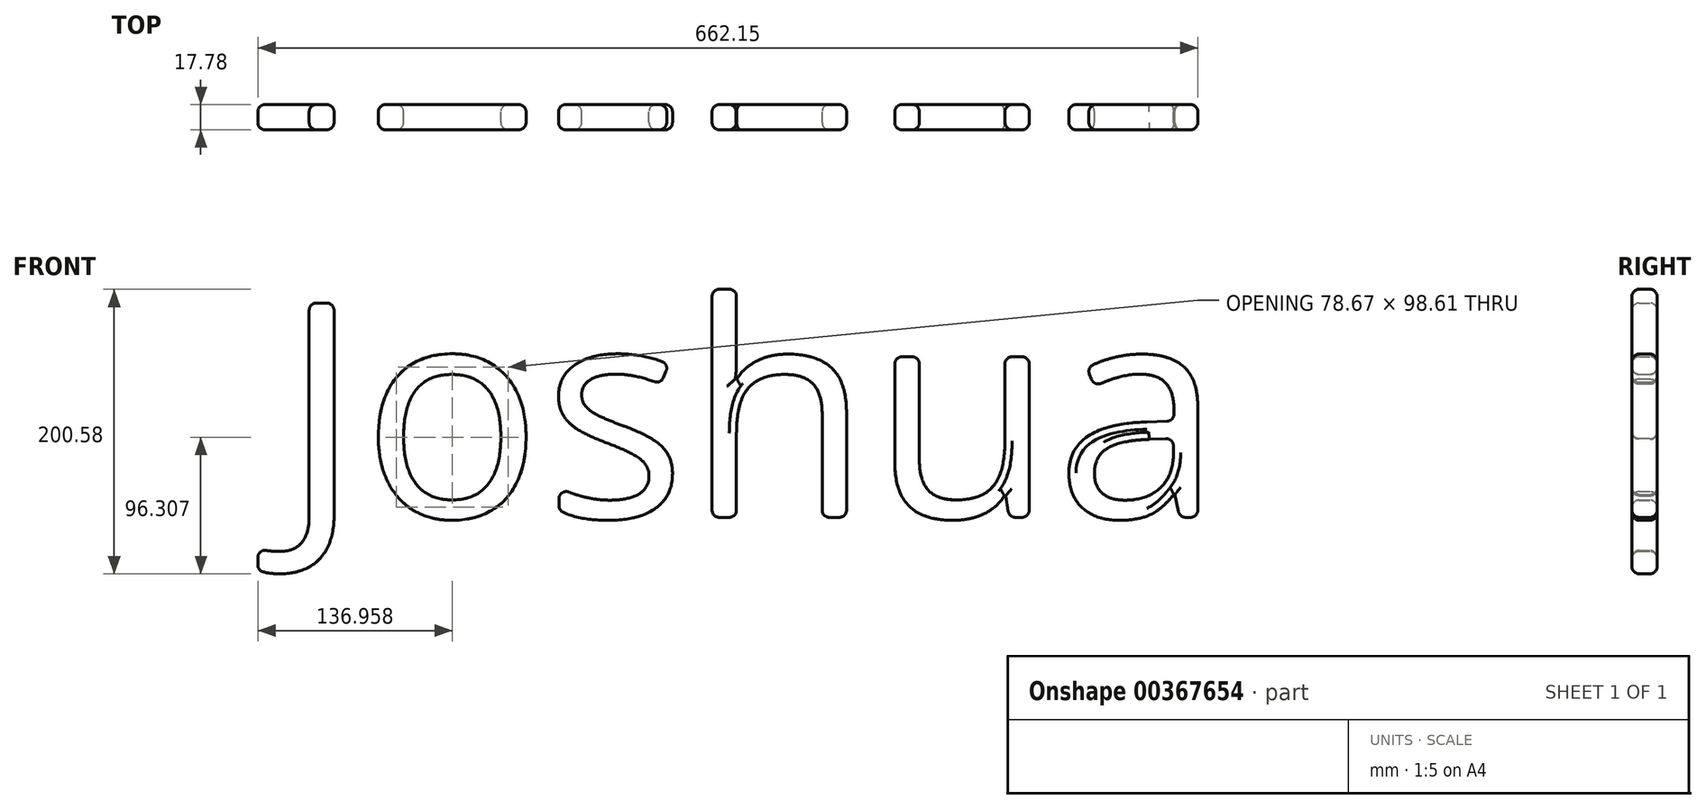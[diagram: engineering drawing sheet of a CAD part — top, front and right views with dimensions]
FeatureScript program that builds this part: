
annotation { "Feature Type Name" : "Feature", "Feature Type Description" : "" }
export const myFeature = defineFeature(function(context is Context, id is Id, definition is map)
    precondition{}
    {
        {
            var Q0;
            Q0=qCreatedBy(makeId("Front.planeOp"),FACE);
            var sketch = newSketch(context, id + "F0", { "sketchPlane" : qUnion([Q0])});
            skText(sketch, "E0", { "text": "Joshua", "fontName": "OpenSans-Regular.ttf"});
            const initialGuessF0  = {"E0": [-0.30372, -0.07697, 1, 0, 0.15237]};
            skSetInitialGuess(sketch, initialGuessF0);
            skSolve(sketch);
        }
        {
            var Q0;
            Q0=makeQuery(id+"F0.imprint","IMPRINT",FACE,{"disambiguationData":[TD([[makeQuery(id+"F0.imprint","IMPRINT",EDGE,{"derivedFrom":sQuery(id+"F0.wireOp",EDGE,"E0.sketch_text.stroke-0")}),-1.0]])]});
            var Q1;
            Q1=makeQuery(id+"F0.imprint","IMPRINT",FACE,{"disambiguationData":[TD([[makeQuery(id+"F0.imprint","IMPRINT",EDGE,{"derivedFrom":sQuery(id+"F0.wireOp",EDGE,"E0.sketch_text.stroke-10")}),-1.0]])]});
            var Q2;
            Q2=makeQuery(id+"F0.imprint","IMPRINT",FACE,{"disambiguationData":[TD([[makeQuery(id+"F0.imprint","IMPRINT",EDGE,{"derivedFrom":sQuery(id+"F0.wireOp",EDGE,"E0.sketch_text.stroke-27")}),-1.0]])]});
            var Q3;
            Q3=makeQuery(id+"F0.imprint","IMPRINT",FACE,{"disambiguationData":[TD([[makeQuery(id+"F0.imprint","IMPRINT",EDGE,{"derivedFrom":sQuery(id+"F0.wireOp",EDGE,"E0.sketch_text.stroke-52")}),-1.0]])]});
            var Q4;
            Q4=makeQuery(id+"F0.imprint","IMPRINT",FACE,{"disambiguationData":[TD([[makeQuery(id+"F0.imprint","IMPRINT",EDGE,{"derivedFrom":sQuery(id+"F0.wireOp",EDGE,"E0.sketch_text.stroke-70")}),-1.0]])]});
            var Q5;
            Q5=makeQuery(id+"F0.imprint","IMPRINT",FACE,{"disambiguationData":[TD([[makeQuery(id+"F0.imprint","IMPRINT",EDGE,{"derivedFrom":sQuery(id+"F0.wireOp",EDGE,"E0.sketch_text.stroke-87")}),-1.0]])]});
            extrude(context, id + "F1", {"entities" : qUnion([Q0, Q1, Q2, Q3, Q4, Q5]), "depth" : 17.78 * mm});
        }
        {
            var Q0;
            Q0=makeQuery(id+"F1.opExtrude","SWEPT_EDGE",EDGE,{"disambiguationData":[OSD([sQuery(id+"F0.wireOp",EDGE,"E0.sketch_text.stroke-5"),sQuery(id+"F0.wireOp",EDGE,"E0.sketch_text.stroke-6")])]});
            var Q1;
            Q1=makeQuery(id+"F1.opExtrude","SWEPT_EDGE",EDGE,{"disambiguationData":[OSD([sQuery(id+"F0.wireOp",EDGE,"E0.sketch_text.stroke-6"),sQuery(id+"F0.wireOp",EDGE,"E0.sketch_text.stroke-7")])]});
            var Q2;
            Q2=makeQuery(id+"F1.opExtrude","CAP_EDGE",EDGE,{"disambiguationData":[OSD([sQuery(id+"F0.wireOp",EDGE,"E0.sketch_text.stroke-0")])],"isStart":false});
            var Q3;
            Q3=makeQuery(id+"F1.opExtrude","CAP_EDGE",EDGE,{"disambiguationData":[OSD([sQuery(id+"F0.wireOp",EDGE,"E0.sketch_text.stroke-2")])],"isStart":true});
            var Q4;
            Q4=makeQuery(id+"F1.opExtrude","CAP_EDGE",EDGE,{"disambiguationData":[OSD([sQuery(id+"F0.wireOp",EDGE,"E0.sketch_text.stroke-2")])],"isStart":false});
            var Q5;
            Q5=makeQuery(id+"F1.opExtrude","SWEPT_EDGE",EDGE,{"disambiguationData":[OSD([sQuery(id+"F0.wireOp",EDGE,"E0.sketch_text.stroke-0"),sQuery(id+"F0.wireOp",EDGE,"E0.sketch_text.stroke-9")])]});
            var Q6;
            Q6=makeQuery(id+"F1.opExtrude","SWEPT_EDGE",EDGE,{"disambiguationData":[OSD([sQuery(id+"F0.wireOp",EDGE,"E0.sketch_text.stroke-1"),sQuery(id+"F0.wireOp",EDGE,"E0.sketch_text.stroke-2")])]});
            var Q7;
            Q7=makeQuery(id+"F1.opExtrude","SWEPT_EDGE",EDGE,{"disambiguationData":[OSD([sQuery(id+"F0.wireOp",EDGE,"E0.sketch_text.stroke-2"),sQuery(id+"F0.wireOp",EDGE,"E0.sketch_text.stroke-3")])]});
            var Q8;
            Q8=makeQuery(id+"F1.opExtrude","SWEPT_EDGE",EDGE,{"disambiguationData":[OSD([sQuery(id+"F0.wireOp",EDGE,"E0.sketch_text.stroke-3"),sQuery(id+"F0.wireOp",EDGE,"E0.sketch_text.stroke-4")])]});
            var Q9;
            Q9=makeQuery(id+"F1.opExtrude","SWEPT_EDGE",EDGE,{"disambiguationData":[OSD([sQuery(id+"F0.wireOp",EDGE,"E0.sketch_text.stroke-4"),sQuery(id+"F0.wireOp",EDGE,"E0.sketch_text.stroke-5")])]});
            var Q10;
            Q10=makeQuery(id+"F1.opExtrude","CAP_EDGE",EDGE,{"disambiguationData":[OSD([sQuery(id+"F0.wireOp",EDGE,"E0.sketch_text.stroke-5")])],"isStart":false});
            var Q11;
            Q11=makeQuery(id+"F1.opExtrude","CAP_EDGE",EDGE,{"disambiguationData":[OSD([sQuery(id+"F0.wireOp",EDGE,"E0.sketch_text.stroke-6")])],"isStart":true});
            var Q12;
            Q12=makeQuery(id+"F1.opExtrude","CAP_EDGE",EDGE,{"disambiguationData":[OSD([sQuery(id+"F0.wireOp",EDGE,"E0.sketch_text.stroke-6")])],"isStart":false});
            var Q13;
            Q13=makeQuery(id+"F1.opExtrude","CAP_EDGE",EDGE,{"disambiguationData":[OSD([sQuery(id+"F0.wireOp",EDGE,"E0.sketch_text.stroke-7")])],"isStart":true});
            var Q14;
            Q14=makeQuery(id+"F1.opExtrude","CAP_EDGE",EDGE,{"disambiguationData":[OSD([sQuery(id+"F0.wireOp",EDGE,"E0.sketch_text.stroke-7")])],"isStart":false});
            var Q15;
            Q15=makeQuery(id+"F1.opExtrude","CAP_EDGE",EDGE,{"disambiguationData":[OSD([sQuery(id+"F0.wireOp",EDGE,"E0.sketch_text.stroke-0")])],"isStart":true});
            var Q16;
            Q16=makeQuery(id+"F1.opExtrude","CAP_EDGE",EDGE,{"disambiguationData":[OSD([sQuery(id+"F0.wireOp",EDGE,"E0.sketch_text.stroke-8")])],"isStart":false});
            var Q17;
            Q17=makeQuery(id+"F1.opExtrude","CAP_EDGE",EDGE,{"disambiguationData":[OSD([sQuery(id+"F0.wireOp",EDGE,"E0.sketch_text.stroke-9")])],"isStart":true});
            var Q18;
            Q18=makeQuery(id+"F1.opExtrude","CAP_EDGE",EDGE,{"disambiguationData":[OSD([sQuery(id+"F0.wireOp",EDGE,"E0.sketch_text.stroke-9")])],"isStart":false});
            var Q19;
            Q19=makeQuery(id+"F1.opExtrude","CAP_EDGE",EDGE,{"disambiguationData":[OSD([sQuery(id+"F0.wireOp",EDGE,"E0.sketch_text.stroke-3")])],"isStart":true});
            var Q20;
            Q20=makeQuery(id+"F1.opExtrude","CAP_EDGE",EDGE,{"disambiguationData":[OSD([sQuery(id+"F0.wireOp",EDGE,"E0.sketch_text.stroke-3")])],"isStart":false});
            var Q21;
            Q21=makeQuery(id+"F1.opExtrude","CAP_EDGE",EDGE,{"disambiguationData":[OSD([sQuery(id+"F0.wireOp",EDGE,"E0.sketch_text.stroke-4")])],"isStart":true});
            var Q22;
            Q22=makeQuery(id+"F1.opExtrude","CAP_EDGE",EDGE,{"disambiguationData":[OSD([sQuery(id+"F0.wireOp",EDGE,"E0.sketch_text.stroke-4")])],"isStart":false});
            var Q23;
            Q23=makeQuery(id+"F1.opExtrude","CAP_EDGE",EDGE,{"disambiguationData":[OSD([sQuery(id+"F0.wireOp",EDGE,"E0.sketch_text.stroke-5")])],"isStart":true});
            var Q24;
            Q24=makeQuery(id+"F1.opExtrude","SWEPT_EDGE",EDGE,{"disambiguationData":[OSD([sQuery(id+"F0.wireOp",EDGE,"E0.sketch_text.stroke-0"),sQuery(id+"F0.wireOp",EDGE,"E0.sketch_text.stroke-1")])]});
            var Q25;
            Q25=makeQuery(id+"F1.opExtrude","SWEPT_EDGE",EDGE,{"disambiguationData":[OSD([sQuery(id+"F0.wireOp",EDGE,"E0.sketch_text.stroke-7"),sQuery(id+"F0.wireOp",EDGE,"E0.sketch_text.stroke-8")])]});
            var Q26;
            Q26=makeQuery(id+"F1.opExtrude","SWEPT_EDGE",EDGE,{"disambiguationData":[OSD([sQuery(id+"F0.wireOp",EDGE,"E0.sketch_text.stroke-8"),sQuery(id+"F0.wireOp",EDGE,"E0.sketch_text.stroke-9")])]});
            var Q27;
            Q27=makeQuery(id+"F1.opExtrude","CAP_EDGE",EDGE,{"disambiguationData":[OSD([sQuery(id+"F0.wireOp",EDGE,"E0.sketch_text.stroke-8")])],"isStart":true});
            var Q28;
            Q28=makeQuery(id+"F1.opExtrude","CAP_EDGE",EDGE,{"disambiguationData":[OSD([sQuery(id+"F0.wireOp",EDGE,"E0.sketch_text.stroke-1")])],"isStart":true});
            var Q29;
            Q29=makeQuery(id+"F1.opExtrude","CAP_EDGE",EDGE,{"disambiguationData":[OSD([sQuery(id+"F0.wireOp",EDGE,"E0.sketch_text.stroke-1")])],"isStart":false});
            fillet(context, id + "F2", {"entities" : qUnion([Q0, Q1, Q2, Q3, Q4, Q5, Q6, Q7, Q8, Q9, Q10, Q11, Q12, Q13, Q14, Q15, Q16, Q17, Q18, Q19, Q20, Q21, Q22, Q23, Q24, Q25, Q26, Q27, Q28, Q29]), "radius" : 5.08 * mm, "tangentPropagation" : true, "allowEdgeOverflow" : false});
        }
        {
            var Q0;
            Q0=makeQuery(id+"F1.opExtrude","CAP_EDGE",EDGE,{"disambiguationData":[OSD([sQuery(id+"F0.wireOp",EDGE,"E0.sketch_text.stroke-22")])],"isStart":false});
            var Q1;
            Q1=makeQuery(id+"F1.opExtrude","CAP_EDGE",EDGE,{"disambiguationData":[OSD([sQuery(id+"F0.wireOp",EDGE,"E0.sketch_text.stroke-15")])],"isStart":false});
            var Q2;
            Q2=makeQuery(id+"F1.opExtrude","CAP_EDGE",EDGE,{"disambiguationData":[OSD([sQuery(id+"F0.wireOp",EDGE,"E0.sketch_text.stroke-23")])],"isStart":false});
            var Q3;
            Q3=makeQuery(id+"F1.opExtrude","CAP_EDGE",EDGE,{"disambiguationData":[OSD([sQuery(id+"F0.wireOp",EDGE,"E0.sketch_text.stroke-16")])],"isStart":true});
            var Q4;
            Q4=makeQuery(id+"F1.opExtrude","CAP_EDGE",EDGE,{"disambiguationData":[OSD([sQuery(id+"F0.wireOp",EDGE,"E0.sketch_text.stroke-16")])],"isStart":false});
            var Q5;
            Q5=makeQuery(id+"F1.opExtrude","CAP_EDGE",EDGE,{"disambiguationData":[OSD([sQuery(id+"F0.wireOp",EDGE,"E0.sketch_text.stroke-17")])],"isStart":true});
            var Q6;
            Q6=makeQuery(id+"F1.opExtrude","CAP_EDGE",EDGE,{"disambiguationData":[OSD([sQuery(id+"F0.wireOp",EDGE,"E0.sketch_text.stroke-17")])],"isStart":false});
            var Q7;
            Q7=makeQuery(id+"F1.opExtrude","CAP_EDGE",EDGE,{"disambiguationData":[OSD([sQuery(id+"F0.wireOp",EDGE,"E0.sketch_text.stroke-10")])],"isStart":false});
            var Q8;
            Q8=makeQuery(id+"F1.opExtrude","CAP_EDGE",EDGE,{"disambiguationData":[OSD([sQuery(id+"F0.wireOp",EDGE,"E0.sketch_text.stroke-18")])],"isStart":false});
            var Q9;
            Q9=makeQuery(id+"F1.opExtrude","CAP_EDGE",EDGE,{"disambiguationData":[OSD([sQuery(id+"F0.wireOp",EDGE,"E0.sketch_text.stroke-11")])],"isStart":false});
            var Q10;
            Q10=makeQuery(id+"F1.opExtrude","CAP_EDGE",EDGE,{"disambiguationData":[OSD([sQuery(id+"F0.wireOp",EDGE,"E0.sketch_text.stroke-12")])],"isStart":false});
            var Q11;
            Q11=makeQuery(id+"F1.opExtrude","CAP_EDGE",EDGE,{"disambiguationData":[OSD([sQuery(id+"F0.wireOp",EDGE,"E0.sketch_text.stroke-21")])],"isStart":true});
            var Q12;
            Q12=makeQuery(id+"F1.opExtrude","CAP_EDGE",EDGE,{"disambiguationData":[OSD([sQuery(id+"F0.wireOp",EDGE,"E0.sketch_text.stroke-15")])],"isStart":true});
            var Q13;
            Q13=makeQuery(id+"F1.opExtrude","SWEPT_EDGE",EDGE,{"disambiguationData":[OSD([sQuery(id+"F0.wireOp",EDGE,"E0.sketch_text.stroke-15"),sQuery(id+"F0.wireOp",EDGE,"E0.sketch_text.stroke-16")])]});
            var Q14;
            Q14=makeQuery(id+"F1.opExtrude","CAP_EDGE",EDGE,{"disambiguationData":[OSD([sQuery(id+"F0.wireOp",EDGE,"E0.sketch_text.stroke-14")])],"isStart":false});
            var Q15;
            Q15=makeQuery(id+"F1.opExtrude","CAP_EDGE",EDGE,{"disambiguationData":[OSD([sQuery(id+"F0.wireOp",EDGE,"E0.sketch_text.stroke-23")])],"isStart":true});
            var Q16;
            Q16=makeQuery(id+"F1.opExtrude","SWEPT_EDGE",EDGE,{"disambiguationData":[OSD([sQuery(id+"F0.wireOp",EDGE,"E0.sketch_text.stroke-16"),sQuery(id+"F0.wireOp",EDGE,"E0.sketch_text.stroke-17")])]});
            var Q17;
            Q17=makeQuery(id+"F1.opExtrude","SWEPT_EDGE",EDGE,{"disambiguationData":[OSD([sQuery(id+"F0.wireOp",EDGE,"E0.sketch_text.stroke-17"),sQuery(id+"F0.wireOp",EDGE,"E0.sketch_text.stroke-18")])]});
            var Q18;
            Q18=makeQuery(id+"F1.opExtrude","CAP_EDGE",EDGE,{"disambiguationData":[OSD([sQuery(id+"F0.wireOp",EDGE,"E0.sketch_text.stroke-24")])],"isStart":true});
            var Q19;
            Q19=makeQuery(id+"F1.opExtrude","SWEPT_EDGE",EDGE,{"disambiguationData":[OSD([sQuery(id+"F0.wireOp",EDGE,"E0.sketch_text.stroke-19"),sQuery(id+"F0.wireOp",EDGE,"E0.sketch_text.stroke-26")])]});
            var Q20;
            Q20=makeQuery(id+"F1.opExtrude","CAP_EDGE",EDGE,{"disambiguationData":[OSD([sQuery(id+"F0.wireOp",EDGE,"E0.sketch_text.stroke-24")])],"isStart":false});
            var Q21;
            Q21=makeQuery(id+"F1.opExtrude","SWEPT_EDGE",EDGE,{"disambiguationData":[OSD([sQuery(id+"F0.wireOp",EDGE,"E0.sketch_text.stroke-19"),sQuery(id+"F0.wireOp",EDGE,"E0.sketch_text.stroke-20")])]});
            var Q22;
            Q22=makeQuery(id+"F1.opExtrude","CAP_EDGE",EDGE,{"disambiguationData":[OSD([sQuery(id+"F0.wireOp",EDGE,"E0.sketch_text.stroke-25")])],"isStart":true});
            var Q23;
            Q23=makeQuery(id+"F1.opExtrude","SWEPT_EDGE",EDGE,{"disambiguationData":[OSD([sQuery(id+"F0.wireOp",EDGE,"E0.sketch_text.stroke-14"),sQuery(id+"F0.wireOp",EDGE,"E0.sketch_text.stroke-15")])]});
            var Q24;
            Q24=makeQuery(id+"F1.opExtrude","SWEPT_EDGE",EDGE,{"disambiguationData":[OSD([sQuery(id+"F0.wireOp",EDGE,"E0.sketch_text.stroke-10"),sQuery(id+"F0.wireOp",EDGE,"E0.sketch_text.stroke-18")])]});
            var Q25;
            Q25=makeQuery(id+"F1.opExtrude","SWEPT_EDGE",EDGE,{"disambiguationData":[OSD([sQuery(id+"F0.wireOp",EDGE,"E0.sketch_text.stroke-10"),sQuery(id+"F0.wireOp",EDGE,"E0.sketch_text.stroke-11")])]});
            var Q26;
            Q26=makeQuery(id+"F1.opExtrude","SWEPT_EDGE",EDGE,{"disambiguationData":[OSD([sQuery(id+"F0.wireOp",EDGE,"E0.sketch_text.stroke-20"),sQuery(id+"F0.wireOp",EDGE,"E0.sketch_text.stroke-21")])]});
            var Q27;
            Q27=makeQuery(id+"F1.opExtrude","CAP_EDGE",EDGE,{"disambiguationData":[OSD([sQuery(id+"F0.wireOp",EDGE,"E0.sketch_text.stroke-25")])],"isStart":false});
            var Q28;
            Q28=makeQuery(id+"F1.opExtrude","CAP_EDGE",EDGE,{"disambiguationData":[OSD([sQuery(id+"F0.wireOp",EDGE,"E0.sketch_text.stroke-13")])],"isStart":false});
            var Q29;
            Q29=makeQuery(id+"F1.opExtrude","CAP_EDGE",EDGE,{"disambiguationData":[OSD([sQuery(id+"F0.wireOp",EDGE,"E0.sketch_text.stroke-21")])],"isStart":false});
            var Q30;
            Q30=makeQuery(id+"F1.opExtrude","SWEPT_EDGE",EDGE,{"disambiguationData":[OSD([sQuery(id+"F0.wireOp",EDGE,"E0.sketch_text.stroke-21"),sQuery(id+"F0.wireOp",EDGE,"E0.sketch_text.stroke-22")])]});
            var Q31;
            Q31=makeQuery(id+"F1.opExtrude","CAP_EDGE",EDGE,{"disambiguationData":[OSD([sQuery(id+"F0.wireOp",EDGE,"E0.sketch_text.stroke-10")])],"isStart":true});
            var Q32;
            Q32=makeQuery(id+"F1.opExtrude","CAP_EDGE",EDGE,{"disambiguationData":[OSD([sQuery(id+"F0.wireOp",EDGE,"E0.sketch_text.stroke-18")])],"isStart":true});
            var Q33;
            Q33=makeQuery(id+"F1.opExtrude","CAP_EDGE",EDGE,{"disambiguationData":[OSD([sQuery(id+"F0.wireOp",EDGE,"E0.sketch_text.stroke-26")])],"isStart":true});
            var Q34;
            Q34=makeQuery(id+"F1.opExtrude","CAP_EDGE",EDGE,{"disambiguationData":[OSD([sQuery(id+"F0.wireOp",EDGE,"E0.sketch_text.stroke-14")])],"isStart":true});
            var Q35;
            Q35=makeQuery(id+"F1.opExtrude","CAP_EDGE",EDGE,{"disambiguationData":[OSD([sQuery(id+"F0.wireOp",EDGE,"E0.sketch_text.stroke-22")])],"isStart":true});
            var Q36;
            Q36=makeQuery(id+"F1.opExtrude","SWEPT_EDGE",EDGE,{"disambiguationData":[OSD([sQuery(id+"F0.wireOp",EDGE,"E0.sketch_text.stroke-22"),sQuery(id+"F0.wireOp",EDGE,"E0.sketch_text.stroke-23")])]});
            var Q37;
            Q37=makeQuery(id+"F1.opExtrude","CAP_EDGE",EDGE,{"disambiguationData":[OSD([sQuery(id+"F0.wireOp",EDGE,"E0.sketch_text.stroke-26")])],"isStart":false});
            var Q38;
            Q38=makeQuery(id+"F1.opExtrude","SWEPT_EDGE",EDGE,{"disambiguationData":[OSD([sQuery(id+"F0.wireOp",EDGE,"E0.sketch_text.stroke-23"),sQuery(id+"F0.wireOp",EDGE,"E0.sketch_text.stroke-24")])]});
            var Q39;
            Q39=makeQuery(id+"F1.opExtrude","CAP_EDGE",EDGE,{"disambiguationData":[OSD([sQuery(id+"F0.wireOp",EDGE,"E0.sketch_text.stroke-11")])],"isStart":true});
            var Q40;
            Q40=makeQuery(id+"F1.opExtrude","CAP_EDGE",EDGE,{"disambiguationData":[OSD([sQuery(id+"F0.wireOp",EDGE,"E0.sketch_text.stroke-19")])],"isStart":true});
            var Q41;
            Q41=makeQuery(id+"F1.opExtrude","SWEPT_EDGE",EDGE,{"disambiguationData":[OSD([sQuery(id+"F0.wireOp",EDGE,"E0.sketch_text.stroke-24"),sQuery(id+"F0.wireOp",EDGE,"E0.sketch_text.stroke-25")])]});
            var Q42;
            Q42=makeQuery(id+"F1.opExtrude","CAP_EDGE",EDGE,{"disambiguationData":[OSD([sQuery(id+"F0.wireOp",EDGE,"E0.sketch_text.stroke-19")])],"isStart":false});
            var Q43;
            Q43=makeQuery(id+"F1.opExtrude","SWEPT_EDGE",EDGE,{"disambiguationData":[OSD([sQuery(id+"F0.wireOp",EDGE,"E0.sketch_text.stroke-25"),sQuery(id+"F0.wireOp",EDGE,"E0.sketch_text.stroke-26")])]});
            var Q44;
            Q44=makeQuery(id+"F1.opExtrude","CAP_EDGE",EDGE,{"disambiguationData":[OSD([sQuery(id+"F0.wireOp",EDGE,"E0.sketch_text.stroke-12")])],"isStart":true});
            var Q45;
            Q45=makeQuery(id+"F1.opExtrude","CAP_EDGE",EDGE,{"disambiguationData":[OSD([sQuery(id+"F0.wireOp",EDGE,"E0.sketch_text.stroke-20")])],"isStart":true});
            var Q46;
            Q46=makeQuery(id+"F1.opExtrude","CAP_EDGE",EDGE,{"disambiguationData":[OSD([sQuery(id+"F0.wireOp",EDGE,"E0.sketch_text.stroke-20")])],"isStart":false});
            var Q47;
            Q47=makeQuery(id+"F1.opExtrude","SWEPT_EDGE",EDGE,{"disambiguationData":[OSD([sQuery(id+"F0.wireOp",EDGE,"E0.sketch_text.stroke-12"),sQuery(id+"F0.wireOp",EDGE,"E0.sketch_text.stroke-13")])]});
            var Q48;
            Q48=makeQuery(id+"F1.opExtrude","SWEPT_EDGE",EDGE,{"disambiguationData":[OSD([sQuery(id+"F0.wireOp",EDGE,"E0.sketch_text.stroke-13"),sQuery(id+"F0.wireOp",EDGE,"E0.sketch_text.stroke-14")])]});
            var Q49;
            Q49=makeQuery(id+"F1.opExtrude","SWEPT_EDGE",EDGE,{"disambiguationData":[OSD([sQuery(id+"F0.wireOp",EDGE,"E0.sketch_text.stroke-11"),sQuery(id+"F0.wireOp",EDGE,"E0.sketch_text.stroke-12")])]});
            var Q50;
            Q50=makeQuery(id+"F1.opExtrude","CAP_EDGE",EDGE,{"disambiguationData":[OSD([sQuery(id+"F0.wireOp",EDGE,"E0.sketch_text.stroke-13")])],"isStart":true});
            fillet(context, id + "F3", {"entities" : qUnion([Q0, Q1, Q2, Q3, Q4, Q5, Q6, Q7, Q8, Q9, Q10, Q11, Q12, Q13, Q14, Q15, Q16, Q17, Q18, Q19, Q20, Q21, Q22, Q23, Q24, Q25, Q26, Q27, Q28, Q29, Q30, Q31, Q32, Q33, Q34, Q35, Q36, Q37, Q38, Q39, Q40, Q41, Q42, Q43, Q44, Q45, Q46, Q47, Q48, Q49, Q50]), "radius" : 5.08 * mm, "tangentPropagation" : true, "allowEdgeOverflow" : false});
        }
        {
            var Q0;
            Q0=makeQuery(id+"F1.opExtrude","CAP_EDGE",EDGE,{"disambiguationData":[OSD([sQuery(id+"F0.wireOp",EDGE,"E0.sketch_text.stroke-29")])],"isStart":false});
            var Q1;
            Q1=makeQuery(id+"F1.opExtrude","CAP_EDGE",EDGE,{"disambiguationData":[OSD([sQuery(id+"F0.wireOp",EDGE,"E0.sketch_text.stroke-37")])],"isStart":false});
            var Q2;
            Q2=makeQuery(id+"F1.opExtrude","CAP_EDGE",EDGE,{"disambiguationData":[OSD([sQuery(id+"F0.wireOp",EDGE,"E0.sketch_text.stroke-31")])],"isStart":false});
            var Q3;
            Q3=makeQuery(id+"F1.opExtrude","CAP_EDGE",EDGE,{"disambiguationData":[OSD([sQuery(id+"F0.wireOp",EDGE,"E0.sketch_text.stroke-32")])],"isStart":false});
            var Q4;
            Q4=makeQuery(id+"F1.opExtrude","CAP_EDGE",EDGE,{"disambiguationData":[OSD([sQuery(id+"F0.wireOp",EDGE,"E0.sketch_text.stroke-33")])],"isStart":false});
            var Q5;
            Q5=makeQuery(id+"F1.opExtrude","CAP_EDGE",EDGE,{"disambiguationData":[OSD([sQuery(id+"F0.wireOp",EDGE,"E0.sketch_text.stroke-41")])],"isStart":false});
            var Q6;
            Q6=makeQuery(id+"F1.opExtrude","CAP_EDGE",EDGE,{"disambiguationData":[OSD([sQuery(id+"F0.wireOp",EDGE,"E0.sketch_text.stroke-49")])],"isStart":false});
            var Q7;
            Q7=makeQuery(id+"F1.opExtrude","CAP_EDGE",EDGE,{"disambiguationData":[OSD([sQuery(id+"F0.wireOp",EDGE,"E0.sketch_text.stroke-42")])],"isStart":false});
            var Q8;
            Q8=makeQuery(id+"F1.opExtrude","CAP_EDGE",EDGE,{"disambiguationData":[OSD([sQuery(id+"F0.wireOp",EDGE,"E0.sketch_text.stroke-50")])],"isStart":false});
            var Q9;
            Q9=makeQuery(id+"F1.opExtrude","CAP_EDGE",EDGE,{"disambiguationData":[OSD([sQuery(id+"F0.wireOp",EDGE,"E0.sketch_text.stroke-28")])],"isStart":false});
            var Q10;
            Q10=makeQuery(id+"F1.opExtrude","CAP_EDGE",EDGE,{"disambiguationData":[OSD([sQuery(id+"F0.wireOp",EDGE,"E0.sketch_text.stroke-36")])],"isStart":false});
            var Q11;
            Q11=makeQuery(id+"F1.opExtrude","CAP_EDGE",EDGE,{"disambiguationData":[OSD([sQuery(id+"F0.wireOp",EDGE,"E0.sketch_text.stroke-44")])],"isStart":false});
            var Q12;
            Q12=makeQuery(id+"F1.opExtrude","SWEPT_EDGE",EDGE,{"disambiguationData":[OSD([sQuery(id+"F0.wireOp",EDGE,"E0.sketch_text.stroke-28"),sQuery(id+"F0.wireOp",EDGE,"E0.sketch_text.stroke-29")])]});
            var Q13;
            Q13=makeQuery(id+"F1.opExtrude","CAP_EDGE",EDGE,{"disambiguationData":[OSD([sQuery(id+"F0.wireOp",EDGE,"E0.sketch_text.stroke-45")])],"isStart":false});
            var Q14;
            Q14=makeQuery(id+"F1.opExtrude","SWEPT_EDGE",EDGE,{"disambiguationData":[OSD([sQuery(id+"F0.wireOp",EDGE,"E0.sketch_text.stroke-46"),sQuery(id+"F0.wireOp",EDGE,"E0.sketch_text.stroke-47")])]});
            var Q15;
            Q15=makeQuery(id+"F1.opExtrude","CAP_EDGE",EDGE,{"disambiguationData":[OSD([sQuery(id+"F0.wireOp",EDGE,"E0.sketch_text.stroke-38")])],"isStart":false});
            var Q16;
            Q16=makeQuery(id+"F1.opExtrude","CAP_EDGE",EDGE,{"disambiguationData":[OSD([sQuery(id+"F0.wireOp",EDGE,"E0.sketch_text.stroke-46")])],"isStart":false});
            var Q17;
            Q17=makeQuery(id+"F1.opExtrude","SWEPT_EDGE",EDGE,{"disambiguationData":[OSD([sQuery(id+"F0.wireOp",EDGE,"E0.sketch_text.stroke-47"),sQuery(id+"F0.wireOp",EDGE,"E0.sketch_text.stroke-48")])]});
            var Q18;
            Q18=makeQuery(id+"F1.opExtrude","SWEPT_EDGE",EDGE,{"disambiguationData":[OSD([sQuery(id+"F0.wireOp",EDGE,"E0.sketch_text.stroke-32"),sQuery(id+"F0.wireOp",EDGE,"E0.sketch_text.stroke-33")])]});
            var Q19;
            Q19=makeQuery(id+"F1.opExtrude","SWEPT_EDGE",EDGE,{"disambiguationData":[OSD([sQuery(id+"F0.wireOp",EDGE,"E0.sketch_text.stroke-48"),sQuery(id+"F0.wireOp",EDGE,"E0.sketch_text.stroke-49")])]});
            var Q20;
            Q20=makeQuery(id+"F1.opExtrude","CAP_EDGE",EDGE,{"disambiguationData":[OSD([sQuery(id+"F0.wireOp",EDGE,"E0.sketch_text.stroke-39")])],"isStart":false});
            var Q21;
            Q21=makeQuery(id+"F1.opExtrude","CAP_EDGE",EDGE,{"disambiguationData":[OSD([sQuery(id+"F0.wireOp",EDGE,"E0.sketch_text.stroke-47")])],"isStart":false});
            var Q22;
            Q22=makeQuery(id+"F1.opExtrude","SWEPT_EDGE",EDGE,{"disambiguationData":[OSD([sQuery(id+"F0.wireOp",EDGE,"E0.sketch_text.stroke-33"),sQuery(id+"F0.wireOp",EDGE,"E0.sketch_text.stroke-34")])]});
            var Q23;
            Q23=makeQuery(id+"F1.opExtrude","SWEPT_EDGE",EDGE,{"disambiguationData":[OSD([sQuery(id+"F0.wireOp",EDGE,"E0.sketch_text.stroke-49"),sQuery(id+"F0.wireOp",EDGE,"E0.sketch_text.stroke-50")])]});
            var Q24;
            Q24=makeQuery(id+"F1.opExtrude","CAP_EDGE",EDGE,{"disambiguationData":[OSD([sQuery(id+"F0.wireOp",EDGE,"E0.sketch_text.stroke-32")])],"isStart":true});
            var Q25;
            Q25=makeQuery(id+"F1.opExtrude","SWEPT_EDGE",EDGE,{"disambiguationData":[OSD([sQuery(id+"F0.wireOp",EDGE,"E0.sketch_text.stroke-34"),sQuery(id+"F0.wireOp",EDGE,"E0.sketch_text.stroke-35")])]});
            var Q26;
            Q26=makeQuery(id+"F1.opExtrude","SWEPT_EDGE",EDGE,{"disambiguationData":[OSD([sQuery(id+"F0.wireOp",EDGE,"E0.sketch_text.stroke-50"),sQuery(id+"F0.wireOp",EDGE,"E0.sketch_text.stroke-51")])]});
            var Q27;
            Q27=makeQuery(id+"F1.opExtrude","CAP_EDGE",EDGE,{"disambiguationData":[OSD([sQuery(id+"F0.wireOp",EDGE,"E0.sketch_text.stroke-40")])],"isStart":false});
            var Q28;
            Q28=makeQuery(id+"F1.opExtrude","CAP_EDGE",EDGE,{"disambiguationData":[OSD([sQuery(id+"F0.wireOp",EDGE,"E0.sketch_text.stroke-48")])],"isStart":false});
            var Q29;
            Q29=makeQuery(id+"F1.opExtrude","SWEPT_EDGE",EDGE,{"disambiguationData":[OSD([sQuery(id+"F0.wireOp",EDGE,"E0.sketch_text.stroke-35"),sQuery(id+"F0.wireOp",EDGE,"E0.sketch_text.stroke-36")])]});
            var Q30;
            Q30=makeQuery(id+"F1.opExtrude","CAP_EDGE",EDGE,{"disambiguationData":[OSD([sQuery(id+"F0.wireOp",EDGE,"E0.sketch_text.stroke-33")])],"isStart":true});
            var Q31;
            Q31=makeQuery(id+"F1.opExtrude","CAP_EDGE",EDGE,{"disambiguationData":[OSD([sQuery(id+"F0.wireOp",EDGE,"E0.sketch_text.stroke-41")])],"isStart":true});
            var Q32;
            Q32=makeQuery(id+"F1.opExtrude","CAP_EDGE",EDGE,{"disambiguationData":[OSD([sQuery(id+"F0.wireOp",EDGE,"E0.sketch_text.stroke-49")])],"isStart":true});
            var Q33;
            Q33=makeQuery(id+"F1.opExtrude","CAP_EDGE",EDGE,{"disambiguationData":[OSD([sQuery(id+"F0.wireOp",EDGE,"E0.sketch_text.stroke-42")])],"isStart":true});
            var Q34;
            Q34=makeQuery(id+"F1.opExtrude","CAP_EDGE",EDGE,{"disambiguationData":[OSD([sQuery(id+"F0.wireOp",EDGE,"E0.sketch_text.stroke-50")])],"isStart":true});
            var Q35;
            Q35=makeQuery(id+"F1.opExtrude","CAP_EDGE",EDGE,{"disambiguationData":[OSD([sQuery(id+"F0.wireOp",EDGE,"E0.sketch_text.stroke-34")])],"isStart":false});
            var Q36;
            Q36=makeQuery(id+"F1.opExtrude","CAP_EDGE",EDGE,{"disambiguationData":[OSD([sQuery(id+"F0.wireOp",EDGE,"E0.sketch_text.stroke-27")])],"isStart":false});
            var Q37;
            Q37=makeQuery(id+"F1.opExtrude","CAP_EDGE",EDGE,{"disambiguationData":[OSD([sQuery(id+"F0.wireOp",EDGE,"E0.sketch_text.stroke-35")])],"isStart":false});
            var Q38;
            Q38=makeQuery(id+"F1.opExtrude","CAP_EDGE",EDGE,{"disambiguationData":[OSD([sQuery(id+"F0.wireOp",EDGE,"E0.sketch_text.stroke-43")])],"isStart":false});
            var Q39;
            Q39=makeQuery(id+"F1.opExtrude","CAP_EDGE",EDGE,{"disambiguationData":[OSD([sQuery(id+"F0.wireOp",EDGE,"E0.sketch_text.stroke-51")])],"isStart":false});
            var Q40;
            Q40=makeQuery(id+"F1.opExtrude","CAP_EDGE",EDGE,{"disambiguationData":[OSD([sQuery(id+"F0.wireOp",EDGE,"E0.sketch_text.stroke-28")])],"isStart":true});
            var Q41;
            Q41=makeQuery(id+"F1.opExtrude","CAP_EDGE",EDGE,{"disambiguationData":[OSD([sQuery(id+"F0.wireOp",EDGE,"E0.sketch_text.stroke-36")])],"isStart":true});
            var Q42;
            Q42=makeQuery(id+"F1.opExtrude","CAP_EDGE",EDGE,{"disambiguationData":[OSD([sQuery(id+"F0.wireOp",EDGE,"E0.sketch_text.stroke-44")])],"isStart":true});
            var Q43;
            Q43=makeQuery(id+"F1.opExtrude","CAP_EDGE",EDGE,{"disambiguationData":[OSD([sQuery(id+"F0.wireOp",EDGE,"E0.sketch_text.stroke-29")])],"isStart":true});
            var Q44;
            Q44=makeQuery(id+"F1.opExtrude","SWEPT_EDGE",EDGE,{"disambiguationData":[OSD([sQuery(id+"F0.wireOp",EDGE,"E0.sketch_text.stroke-44"),sQuery(id+"F0.wireOp",EDGE,"E0.sketch_text.stroke-45")])]});
            var Q45;
            Q45=makeQuery(id+"F1.opExtrude","SWEPT_EDGE",EDGE,{"disambiguationData":[OSD([sQuery(id+"F0.wireOp",EDGE,"E0.sketch_text.stroke-29"),sQuery(id+"F0.wireOp",EDGE,"E0.sketch_text.stroke-30")])]});
            var Q46;
            Q46=makeQuery(id+"F1.opExtrude","SWEPT_EDGE",EDGE,{"disambiguationData":[OSD([sQuery(id+"F0.wireOp",EDGE,"E0.sketch_text.stroke-45"),sQuery(id+"F0.wireOp",EDGE,"E0.sketch_text.stroke-46")])]});
            var Q47;
            Q47=makeQuery(id+"F1.opExtrude","CAP_EDGE",EDGE,{"disambiguationData":[OSD([sQuery(id+"F0.wireOp",EDGE,"E0.sketch_text.stroke-38")])],"isStart":true});
            var Q48;
            Q48=makeQuery(id+"F1.opExtrude","CAP_EDGE",EDGE,{"disambiguationData":[OSD([sQuery(id+"F0.wireOp",EDGE,"E0.sketch_text.stroke-46")])],"isStart":true});
            var Q49;
            Q49=makeQuery(id+"F1.opExtrude","SWEPT_EDGE",EDGE,{"disambiguationData":[OSD([sQuery(id+"F0.wireOp",EDGE,"E0.sketch_text.stroke-30"),sQuery(id+"F0.wireOp",EDGE,"E0.sketch_text.stroke-31")])]});
            var Q50;
            Q50=makeQuery(id+"F1.opExtrude","CAP_EDGE",EDGE,{"disambiguationData":[OSD([sQuery(id+"F0.wireOp",EDGE,"E0.sketch_text.stroke-30")])],"isStart":false});
            var Q51;
            Q51=makeQuery(id+"F1.opExtrude","SWEPT_EDGE",EDGE,{"disambiguationData":[OSD([sQuery(id+"F0.wireOp",EDGE,"E0.sketch_text.stroke-31"),sQuery(id+"F0.wireOp",EDGE,"E0.sketch_text.stroke-32")])]});
            var Q52;
            Q52=makeQuery(id+"F1.opExtrude","CAP_EDGE",EDGE,{"disambiguationData":[OSD([sQuery(id+"F0.wireOp",EDGE,"E0.sketch_text.stroke-31")])],"isStart":true});
            var Q53;
            Q53=makeQuery(id+"F1.opExtrude","CAP_EDGE",EDGE,{"disambiguationData":[OSD([sQuery(id+"F0.wireOp",EDGE,"E0.sketch_text.stroke-39")])],"isStart":true});
            var Q54;
            Q54=makeQuery(id+"F1.opExtrude","CAP_EDGE",EDGE,{"disambiguationData":[OSD([sQuery(id+"F0.wireOp",EDGE,"E0.sketch_text.stroke-47")])],"isStart":true});
            var Q55;
            Q55=makeQuery(id+"F1.opExtrude","CAP_EDGE",EDGE,{"disambiguationData":[OSD([sQuery(id+"F0.wireOp",EDGE,"E0.sketch_text.stroke-40")])],"isStart":true});
            var Q56;
            Q56=makeQuery(id+"F1.opExtrude","CAP_EDGE",EDGE,{"disambiguationData":[OSD([sQuery(id+"F0.wireOp",EDGE,"E0.sketch_text.stroke-48")])],"isStart":true});
            var Q57;
            Q57=makeQuery(id+"F1.opExtrude","SWEPT_EDGE",EDGE,{"disambiguationData":[OSD([sQuery(id+"F0.wireOp",EDGE,"E0.sketch_text.stroke-36"),sQuery(id+"F0.wireOp",EDGE,"E0.sketch_text.stroke-37")])]});
            var Q58;
            Q58=makeQuery(id+"F1.opExtrude","SWEPT_EDGE",EDGE,{"disambiguationData":[OSD([sQuery(id+"F0.wireOp",EDGE,"E0.sketch_text.stroke-37"),sQuery(id+"F0.wireOp",EDGE,"E0.sketch_text.stroke-38")])]});
            var Q59;
            Q59=makeQuery(id+"F1.opExtrude","CAP_EDGE",EDGE,{"disambiguationData":[OSD([sQuery(id+"F0.wireOp",EDGE,"E0.sketch_text.stroke-34")])],"isStart":true});
            var Q60;
            Q60=makeQuery(id+"F1.opExtrude","SWEPT_EDGE",EDGE,{"disambiguationData":[OSD([sQuery(id+"F0.wireOp",EDGE,"E0.sketch_text.stroke-38"),sQuery(id+"F0.wireOp",EDGE,"E0.sketch_text.stroke-39")])]});
            var Q61;
            Q61=makeQuery(id+"F1.opExtrude","SWEPT_EDGE",EDGE,{"disambiguationData":[OSD([sQuery(id+"F0.wireOp",EDGE,"E0.sketch_text.stroke-39"),sQuery(id+"F0.wireOp",EDGE,"E0.sketch_text.stroke-40")])]});
            var Q62;
            Q62=makeQuery(id+"F1.opExtrude","CAP_EDGE",EDGE,{"disambiguationData":[OSD([sQuery(id+"F0.wireOp",EDGE,"E0.sketch_text.stroke-27")])],"isStart":true});
            var Q63;
            Q63=makeQuery(id+"F1.opExtrude","CAP_EDGE",EDGE,{"disambiguationData":[OSD([sQuery(id+"F0.wireOp",EDGE,"E0.sketch_text.stroke-35")])],"isStart":true});
            var Q64;
            Q64=makeQuery(id+"F1.opExtrude","CAP_EDGE",EDGE,{"disambiguationData":[OSD([sQuery(id+"F0.wireOp",EDGE,"E0.sketch_text.stroke-43")])],"isStart":true});
            var Q65;
            Q65=makeQuery(id+"F1.opExtrude","CAP_EDGE",EDGE,{"disambiguationData":[OSD([sQuery(id+"F0.wireOp",EDGE,"E0.sketch_text.stroke-51")])],"isStart":true});
            var Q66;
            Q66=makeQuery(id+"F1.opExtrude","SWEPT_EDGE",EDGE,{"disambiguationData":[OSD([sQuery(id+"F0.wireOp",EDGE,"E0.sketch_text.stroke-40"),sQuery(id+"F0.wireOp",EDGE,"E0.sketch_text.stroke-41")])]});
            var Q67;
            Q67=makeQuery(id+"F1.opExtrude","SWEPT_EDGE",EDGE,{"disambiguationData":[OSD([sQuery(id+"F0.wireOp",EDGE,"E0.sketch_text.stroke-41"),sQuery(id+"F0.wireOp",EDGE,"E0.sketch_text.stroke-42")])]});
            var Q68;
            Q68=makeQuery(id+"F1.opExtrude","SWEPT_EDGE",EDGE,{"disambiguationData":[OSD([sQuery(id+"F0.wireOp",EDGE,"E0.sketch_text.stroke-27"),sQuery(id+"F0.wireOp",EDGE,"E0.sketch_text.stroke-51")])]});
            var Q69;
            Q69=makeQuery(id+"F1.opExtrude","SWEPT_EDGE",EDGE,{"disambiguationData":[OSD([sQuery(id+"F0.wireOp",EDGE,"E0.sketch_text.stroke-42"),sQuery(id+"F0.wireOp",EDGE,"E0.sketch_text.stroke-43")])]});
            var Q70;
            Q70=makeQuery(id+"F1.opExtrude","SWEPT_EDGE",EDGE,{"disambiguationData":[OSD([sQuery(id+"F0.wireOp",EDGE,"E0.sketch_text.stroke-27"),sQuery(id+"F0.wireOp",EDGE,"E0.sketch_text.stroke-28")])]});
            var Q71;
            Q71=makeQuery(id+"F1.opExtrude","SWEPT_EDGE",EDGE,{"disambiguationData":[OSD([sQuery(id+"F0.wireOp",EDGE,"E0.sketch_text.stroke-43"),sQuery(id+"F0.wireOp",EDGE,"E0.sketch_text.stroke-44")])]});
            var Q72;
            Q72=makeQuery(id+"F1.opExtrude","CAP_EDGE",EDGE,{"disambiguationData":[OSD([sQuery(id+"F0.wireOp",EDGE,"E0.sketch_text.stroke-37")])],"isStart":true});
            var Q73;
            Q73=makeQuery(id+"F1.opExtrude","CAP_EDGE",EDGE,{"disambiguationData":[OSD([sQuery(id+"F0.wireOp",EDGE,"E0.sketch_text.stroke-45")])],"isStart":true});
            var Q74;
            Q74=makeQuery(id+"F1.opExtrude","CAP_EDGE",EDGE,{"disambiguationData":[OSD([sQuery(id+"F0.wireOp",EDGE,"E0.sketch_text.stroke-30")])],"isStart":true});
            fillet(context, id + "F4", {"entities" : qUnion([Q0, Q1, Q2, Q3, Q4, Q5, Q6, Q7, Q8, Q9, Q10, Q11, Q12, Q13, Q14, Q15, Q16, Q17, Q18, Q19, Q20, Q21, Q22, Q23, Q24, Q25, Q26, Q27, Q28, Q29, Q30, Q31, Q32, Q33, Q34, Q35, Q36, Q37, Q38, Q39, Q40, Q41, Q42, Q43, Q44, Q45, Q46, Q47, Q48, Q49, Q50, Q51, Q52, Q53, Q54, Q55, Q56, Q57, Q58, Q59, Q60, Q61, Q62, Q63, Q64, Q65, Q66, Q67, Q68, Q69, Q70, Q71, Q72, Q73, Q74]), "radius" : 5.08 * mm, "tangentPropagation" : true, "allowEdgeOverflow" : false});
        }
        {
            var Q0;
            Q0=makeQuery(id+"F1.opExtrude","CAP_FACE",FACE,{"disambiguationData":[OSD([sQuery(id+"F0.wireOp",EDGE,"E0.sketch_text.stroke-52"),sQuery(id+"F0.wireOp",EDGE,"E0.sketch_text.stroke-53"),sQuery(id+"F0.wireOp",EDGE,"E0.sketch_text.stroke-54"),sQuery(id+"F0.wireOp",EDGE,"E0.sketch_text.stroke-55"),sQuery(id+"F0.wireOp",EDGE,"E0.sketch_text.stroke-56"),sQuery(id+"F0.wireOp",EDGE,"E0.sketch_text.stroke-57"),sQuery(id+"F0.wireOp",EDGE,"E0.sketch_text.stroke-58"),sQuery(id+"F0.wireOp",EDGE,"E0.sketch_text.stroke-59"),sQuery(id+"F0.wireOp",EDGE,"E0.sketch_text.stroke-60"),sQuery(id+"F0.wireOp",EDGE,"E0.sketch_text.stroke-61"),sQuery(id+"F0.wireOp",EDGE,"E0.sketch_text.stroke-62"),sQuery(id+"F0.wireOp",EDGE,"E0.sketch_text.stroke-63"),sQuery(id+"F0.wireOp",EDGE,"E0.sketch_text.stroke-64"),sQuery(id+"F0.wireOp",EDGE,"E0.sketch_text.stroke-65"),sQuery(id+"F0.wireOp",EDGE,"E0.sketch_text.stroke-66"),sQuery(id+"F0.wireOp",EDGE,"E0.sketch_text.stroke-67"),sQuery(id+"F0.wireOp",EDGE,"E0.sketch_text.stroke-68"),sQuery(id+"F0.wireOp",EDGE,"E0.sketch_text.stroke-69")])],"isStart":false});
            var Q1;
            Q1=makeQuery(id+"F1.opExtrude","CAP_FACE",FACE,{"disambiguationData":[OSD([sQuery(id+"F0.wireOp",EDGE,"E0.sketch_text.stroke-52"),sQuery(id+"F0.wireOp",EDGE,"E0.sketch_text.stroke-53"),sQuery(id+"F0.wireOp",EDGE,"E0.sketch_text.stroke-54"),sQuery(id+"F0.wireOp",EDGE,"E0.sketch_text.stroke-55"),sQuery(id+"F0.wireOp",EDGE,"E0.sketch_text.stroke-56"),sQuery(id+"F0.wireOp",EDGE,"E0.sketch_text.stroke-57"),sQuery(id+"F0.wireOp",EDGE,"E0.sketch_text.stroke-58"),sQuery(id+"F0.wireOp",EDGE,"E0.sketch_text.stroke-59"),sQuery(id+"F0.wireOp",EDGE,"E0.sketch_text.stroke-60"),sQuery(id+"F0.wireOp",EDGE,"E0.sketch_text.stroke-61"),sQuery(id+"F0.wireOp",EDGE,"E0.sketch_text.stroke-62"),sQuery(id+"F0.wireOp",EDGE,"E0.sketch_text.stroke-63"),sQuery(id+"F0.wireOp",EDGE,"E0.sketch_text.stroke-64"),sQuery(id+"F0.wireOp",EDGE,"E0.sketch_text.stroke-65"),sQuery(id+"F0.wireOp",EDGE,"E0.sketch_text.stroke-66"),sQuery(id+"F0.wireOp",EDGE,"E0.sketch_text.stroke-67"),sQuery(id+"F0.wireOp",EDGE,"E0.sketch_text.stroke-68"),sQuery(id+"F0.wireOp",EDGE,"E0.sketch_text.stroke-69")])],"isStart":true});
            var Q2;
            Q2=makeQuery(id+"F1.opExtrude","SWEPT_FACE",FACE,{"disambiguationData":[OSD([sQuery(id+"F0.wireOp",EDGE,"E0.sketch_text.stroke-58")])]});
            var Q3;
            Q3=makeQuery(id+"F1.opExtrude","SWEPT_FACE",FACE,{"disambiguationData":[OSD([sQuery(id+"F0.wireOp",EDGE,"E0.sketch_text.stroke-69")])]});
            var Q4;
            Q4=makeQuery(id+"F1.opExtrude","SWEPT_FACE",FACE,{"disambiguationData":[OSD([sQuery(id+"F0.wireOp",EDGE,"E0.sketch_text.stroke-60")])]});
            var Q5;
            Q5=makeQuery(id+"F1.opExtrude","SWEPT_FACE",FACE,{"disambiguationData":[OSD([sQuery(id+"F0.wireOp",EDGE,"E0.sketch_text.stroke-61")])]});
            fillet(context, id + "F5", {"entities" : qUnion([Q0, Q1, Q2, Q3, Q4, Q5]), "radius" : 5.08 * mm, "tangentPropagation" : true, "allowEdgeOverflow" : false});
        }
        {
            var Q0;
            Q0=makeQuery(id+"F1.opExtrude","CAP_FACE",FACE,{"disambiguationData":[OSD([sQuery(id+"F0.wireOp",EDGE,"E0.sketch_text.stroke-70"),sQuery(id+"F0.wireOp",EDGE,"E0.sketch_text.stroke-71"),sQuery(id+"F0.wireOp",EDGE,"E0.sketch_text.stroke-72"),sQuery(id+"F0.wireOp",EDGE,"E0.sketch_text.stroke-73"),sQuery(id+"F0.wireOp",EDGE,"E0.sketch_text.stroke-74"),sQuery(id+"F0.wireOp",EDGE,"E0.sketch_text.stroke-75"),sQuery(id+"F0.wireOp",EDGE,"E0.sketch_text.stroke-76"),sQuery(id+"F0.wireOp",EDGE,"E0.sketch_text.stroke-77"),sQuery(id+"F0.wireOp",EDGE,"E0.sketch_text.stroke-78"),sQuery(id+"F0.wireOp",EDGE,"E0.sketch_text.stroke-79"),sQuery(id+"F0.wireOp",EDGE,"E0.sketch_text.stroke-80"),sQuery(id+"F0.wireOp",EDGE,"E0.sketch_text.stroke-81"),sQuery(id+"F0.wireOp",EDGE,"E0.sketch_text.stroke-82"),sQuery(id+"F0.wireOp",EDGE,"E0.sketch_text.stroke-83"),sQuery(id+"F0.wireOp",EDGE,"E0.sketch_text.stroke-84"),sQuery(id+"F0.wireOp",EDGE,"E0.sketch_text.stroke-85"),sQuery(id+"F0.wireOp",EDGE,"E0.sketch_text.stroke-86")])],"isStart":false});
            var Q1;
            Q1=makeQuery(id+"F1.opExtrude","CAP_FACE",FACE,{"disambiguationData":[OSD([sQuery(id+"F0.wireOp",EDGE,"E0.sketch_text.stroke-70"),sQuery(id+"F0.wireOp",EDGE,"E0.sketch_text.stroke-71"),sQuery(id+"F0.wireOp",EDGE,"E0.sketch_text.stroke-72"),sQuery(id+"F0.wireOp",EDGE,"E0.sketch_text.stroke-73"),sQuery(id+"F0.wireOp",EDGE,"E0.sketch_text.stroke-74"),sQuery(id+"F0.wireOp",EDGE,"E0.sketch_text.stroke-75"),sQuery(id+"F0.wireOp",EDGE,"E0.sketch_text.stroke-76"),sQuery(id+"F0.wireOp",EDGE,"E0.sketch_text.stroke-77"),sQuery(id+"F0.wireOp",EDGE,"E0.sketch_text.stroke-78"),sQuery(id+"F0.wireOp",EDGE,"E0.sketch_text.stroke-79"),sQuery(id+"F0.wireOp",EDGE,"E0.sketch_text.stroke-80"),sQuery(id+"F0.wireOp",EDGE,"E0.sketch_text.stroke-81"),sQuery(id+"F0.wireOp",EDGE,"E0.sketch_text.stroke-82"),sQuery(id+"F0.wireOp",EDGE,"E0.sketch_text.stroke-83"),sQuery(id+"F0.wireOp",EDGE,"E0.sketch_text.stroke-84"),sQuery(id+"F0.wireOp",EDGE,"E0.sketch_text.stroke-85"),sQuery(id+"F0.wireOp",EDGE,"E0.sketch_text.stroke-86")])],"isStart":true});
            var Q2;
            Q2=makeQuery(id+"F1.opExtrude","SWEPT_FACE",FACE,{"disambiguationData":[OSD([sQuery(id+"F0.wireOp",EDGE,"E0.sketch_text.stroke-76")])]});
            var Q3;
            Q3=makeQuery(id+"F1.opExtrude","SWEPT_FACE",FACE,{"disambiguationData":[OSD([sQuery(id+"F0.wireOp",EDGE,"E0.sketch_text.stroke-86")])]});
            var Q4;
            Q4=makeQuery(id+"F1.opExtrude","SWEPT_FACE",FACE,{"disambiguationData":[OSD([sQuery(id+"F0.wireOp",EDGE,"E0.sketch_text.stroke-78")])]});
            var Q5;
            Q5=makeQuery(id+"F1.opExtrude","SWEPT_FACE",FACE,{"disambiguationData":[OSD([sQuery(id+"F0.wireOp",EDGE,"E0.sketch_text.stroke-77")])]});
            var Q6;
            Q6=makeQuery(id+"F1.opExtrude","SWEPT_FACE",FACE,{"disambiguationData":[OSD([sQuery(id+"F0.wireOp",EDGE,"E0.sketch_text.stroke-85")])]});
            var Q7;
            Q7=makeQuery(id+"F1.opExtrude","SWEPT_FACE",FACE,{"disambiguationData":[OSD([sQuery(id+"F0.wireOp",EDGE,"E0.sketch_text.stroke-75")])]});
            fillet(context, id + "F6", {"entities" : qUnion([Q0, Q1, Q2, Q3, Q4, Q5, Q6, Q7]), "radius" : 5.08 * mm, "tangentPropagation" : true, "allowEdgeOverflow" : false});
        }
        {
            var Q0;
            Q0=makeQuery(id+"F1.opExtrude","CAP_FACE",FACE,{"disambiguationData":[OSD([sQuery(id+"F0.wireOp",EDGE,"E0.sketch_text.stroke-87"),sQuery(id+"F0.wireOp",EDGE,"E0.sketch_text.stroke-88"),sQuery(id+"F0.wireOp",EDGE,"E0.sketch_text.stroke-89"),sQuery(id+"F0.wireOp",EDGE,"E0.sketch_text.stroke-90"),sQuery(id+"F0.wireOp",EDGE,"E0.sketch_text.stroke-91"),sQuery(id+"F0.wireOp",EDGE,"E0.sketch_text.stroke-92"),sQuery(id+"F0.wireOp",EDGE,"E0.sketch_text.stroke-93"),sQuery(id+"F0.wireOp",EDGE,"E0.sketch_text.stroke-94"),sQuery(id+"F0.wireOp",EDGE,"E0.sketch_text.stroke-95"),sQuery(id+"F0.wireOp",EDGE,"E0.sketch_text.stroke-96"),sQuery(id+"F0.wireOp",EDGE,"E0.sketch_text.stroke-97"),sQuery(id+"F0.wireOp",EDGE,"E0.sketch_text.stroke-98"),sQuery(id+"F0.wireOp",EDGE,"E0.sketch_text.stroke-99"),sQuery(id+"F0.wireOp",EDGE,"E0.sketch_text.stroke-100"),sQuery(id+"F0.wireOp",EDGE,"E0.sketch_text.stroke-101"),sQuery(id+"F0.wireOp",EDGE,"E0.sketch_text.stroke-102"),sQuery(id+"F0.wireOp",EDGE,"E0.sketch_text.stroke-103"),sQuery(id+"F0.wireOp",EDGE,"E0.sketch_text.stroke-104"),sQuery(id+"F0.wireOp",EDGE,"E0.sketch_text.stroke-105"),sQuery(id+"F0.wireOp",EDGE,"E0.sketch_text.stroke-106"),sQuery(id+"F0.wireOp",EDGE,"E0.sketch_text.stroke-107"),sQuery(id+"F0.wireOp",EDGE,"E0.sketch_text.stroke-108"),sQuery(id+"F0.wireOp",EDGE,"E0.sketch_text.stroke-109"),sQuery(id+"F0.wireOp",EDGE,"E0.sketch_text.stroke-110"),sQuery(id+"F0.wireOp",EDGE,"E0.sketch_text.stroke-111"),sQuery(id+"F0.wireOp",EDGE,"E0.sketch_text.stroke-112"),sQuery(id+"F0.wireOp",EDGE,"E0.sketch_text.stroke-113")])],"isStart":false});
            var Q1;
            Q1=makeQuery(id+"F1.opExtrude","SWEPT_FACE",FACE,{"disambiguationData":[OSD([sQuery(id+"F0.wireOp",EDGE,"E0.sketch_text.stroke-104")])]});
            var Q2;
            Q2=makeQuery(id+"F1.opExtrude","SWEPT_FACE",FACE,{"disambiguationData":[OSD([sQuery(id+"F0.wireOp",EDGE,"E0.sketch_text.stroke-103")])]});
            var Q3;
            Q3=makeQuery(id+"F1.opExtrude","SWEPT_FACE",FACE,{"disambiguationData":[OSD([sQuery(id+"F0.wireOp",EDGE,"E0.sketch_text.stroke-102")])]});
            var Q4;
            Q4=makeQuery(id+"F1.opExtrude","SWEPT_FACE",FACE,{"disambiguationData":[OSD([sQuery(id+"F0.wireOp",EDGE,"E0.sketch_text.stroke-101")])]});
            var Q5;
            Q5=makeQuery(id+"F1.opExtrude","SWEPT_FACE",FACE,{"disambiguationData":[OSD([sQuery(id+"F0.wireOp",EDGE,"E0.sketch_text.stroke-100")])]});
            var Q6;
            Q6=makeQuery(id+"F1.opExtrude","CAP_EDGE",EDGE,{"disambiguationData":[OSD([sQuery(id+"F0.wireOp",EDGE,"E0.sketch_text.stroke-99")])],"isStart":false});
            var Q7;
            Q7=makeQuery(id+"F1.opExtrude","CAP_FACE",FACE,{"disambiguationData":[OSD([sQuery(id+"F0.wireOp",EDGE,"E0.sketch_text.stroke-87"),sQuery(id+"F0.wireOp",EDGE,"E0.sketch_text.stroke-88"),sQuery(id+"F0.wireOp",EDGE,"E0.sketch_text.stroke-89"),sQuery(id+"F0.wireOp",EDGE,"E0.sketch_text.stroke-90"),sQuery(id+"F0.wireOp",EDGE,"E0.sketch_text.stroke-91"),sQuery(id+"F0.wireOp",EDGE,"E0.sketch_text.stroke-92"),sQuery(id+"F0.wireOp",EDGE,"E0.sketch_text.stroke-93"),sQuery(id+"F0.wireOp",EDGE,"E0.sketch_text.stroke-94"),sQuery(id+"F0.wireOp",EDGE,"E0.sketch_text.stroke-95"),sQuery(id+"F0.wireOp",EDGE,"E0.sketch_text.stroke-96"),sQuery(id+"F0.wireOp",EDGE,"E0.sketch_text.stroke-97"),sQuery(id+"F0.wireOp",EDGE,"E0.sketch_text.stroke-98"),sQuery(id+"F0.wireOp",EDGE,"E0.sketch_text.stroke-99"),sQuery(id+"F0.wireOp",EDGE,"E0.sketch_text.stroke-100"),sQuery(id+"F0.wireOp",EDGE,"E0.sketch_text.stroke-101"),sQuery(id+"F0.wireOp",EDGE,"E0.sketch_text.stroke-102"),sQuery(id+"F0.wireOp",EDGE,"E0.sketch_text.stroke-103"),sQuery(id+"F0.wireOp",EDGE,"E0.sketch_text.stroke-104"),sQuery(id+"F0.wireOp",EDGE,"E0.sketch_text.stroke-105"),sQuery(id+"F0.wireOp",EDGE,"E0.sketch_text.stroke-106"),sQuery(id+"F0.wireOp",EDGE,"E0.sketch_text.stroke-107"),sQuery(id+"F0.wireOp",EDGE,"E0.sketch_text.stroke-108"),sQuery(id+"F0.wireOp",EDGE,"E0.sketch_text.stroke-109"),sQuery(id+"F0.wireOp",EDGE,"E0.sketch_text.stroke-110"),sQuery(id+"F0.wireOp",EDGE,"E0.sketch_text.stroke-111"),sQuery(id+"F0.wireOp",EDGE,"E0.sketch_text.stroke-112"),sQuery(id+"F0.wireOp",EDGE,"E0.sketch_text.stroke-113")])],"isStart":true});
            var Q8;
            Q8=makeQuery(id+"F1.opExtrude","SWEPT_FACE",FACE,{"disambiguationData":[OSD([sQuery(id+"F0.wireOp",EDGE,"E0.sketch_text.stroke-99")])]});
            var Q9;
            Q9=makeQuery(id+"F1.opExtrude","SWEPT_FACE",FACE,{"disambiguationData":[OSD([sQuery(id+"F0.wireOp",EDGE,"E0.sketch_text.stroke-105")])]});
            var Q10;
            Q10=makeQuery(id+"F1.opExtrude","SWEPT_FACE",FACE,{"disambiguationData":[OSD([sQuery(id+"F0.wireOp",EDGE,"E0.sketch_text.stroke-92")])]});
            var Q11;
            Q11=makeQuery(id+"F1.opExtrude","SWEPT_FACE",FACE,{"disambiguationData":[OSD([sQuery(id+"F0.wireOp",EDGE,"E0.sketch_text.stroke-91")])]});
            var Q12;
            Q12=makeQuery(id+"F1.opExtrude","SWEPT_FACE",FACE,{"disambiguationData":[OSD([sQuery(id+"F0.wireOp",EDGE,"E0.sketch_text.stroke-90")])]});
            var Q13;
            Q13=makeQuery(id+"F1.opExtrude","CAP_EDGE",EDGE,{"disambiguationData":[OSD([sQuery(id+"F0.wireOp",EDGE,"E0.sketch_text.stroke-93")])],"isStart":true});
            var Q14;
            Q14=makeQuery(id+"F1.opExtrude","SWEPT_FACE",FACE,{"disambiguationData":[OSD([sQuery(id+"F0.wireOp",EDGE,"E0.sketch_text.stroke-94")])]});
            var Q15;
            Q15=makeQuery(id+"F1.opExtrude","SWEPT_FACE",FACE,{"disambiguationData":[OSD([sQuery(id+"F0.wireOp",EDGE,"E0.sketch_text.stroke-93")])]});
            var Q16;
            Q16=makeQuery(id+"F1.opExtrude","SWEPT_EDGE",EDGE,{"disambiguationData":[OSD([sQuery(id+"F0.wireOp",EDGE,"E0.sketch_text.stroke-108"),sQuery(id+"F0.wireOp",EDGE,"E0.sketch_text.stroke-109")])]});
            fillet(context, id + "F7", {"entities" : qUnion([Q0, Q1, Q2, Q3, Q4, Q5, Q6, Q7, Q8, Q9, Q10, Q11, Q12, Q13, Q14, Q15, Q16]), "radius" : 5.08 * mm, "tangentPropagation" : true, "allowEdgeOverflow" : false});
        }
    });
